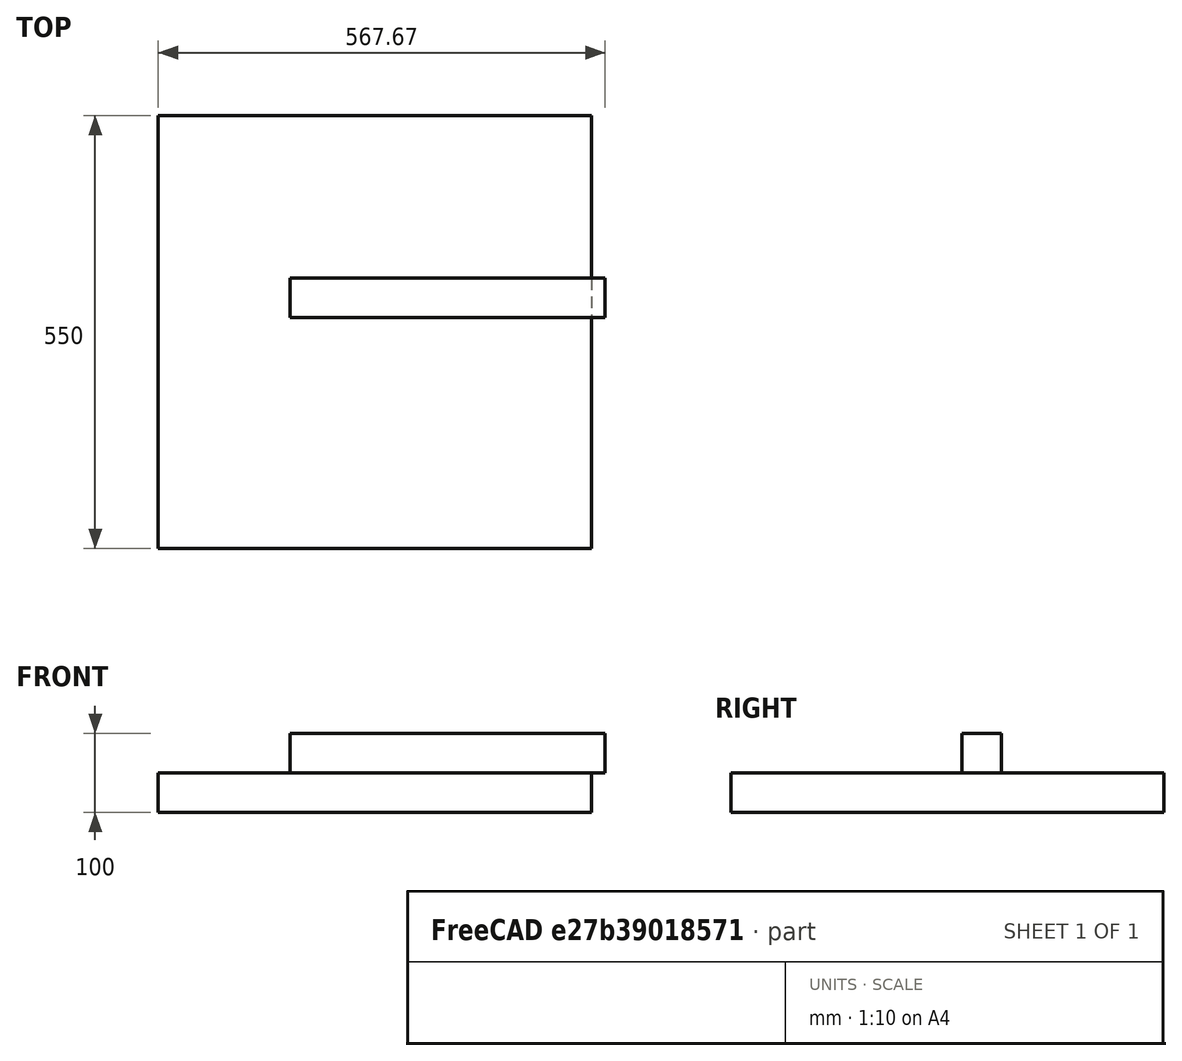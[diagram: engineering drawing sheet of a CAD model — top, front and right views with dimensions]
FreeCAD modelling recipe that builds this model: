
FCSTD DOCUMENT  (FreeCAD 1.0R38806 (Git))
Label: mesa_Ikea
License: All rights reserved
LicenseURL: https://en.wikipedia.org/wiki/All_rights_reserved
objects: App::Link×5, App::FeaturePython×5, Sketcher::SketchObject×2, PartDesign::Pad×2, PartDesign::Body×2, App::Part×2, App::DocumentObjectGroup×1, Assembly::JointGroup×1, Assembly::AssemblyObject×1
note: 12 computed .brp shape members not serialized (recipe doc carries the construction recipe); baked Part::Feature solids carry a one-line shape summary decoded from their .brp

FEATURE [Sketcher::SketchObject] Sketch
  ArcFitTolerance = 1e-06
  AttachmentSupport = -> [YZ_Plane]
  FullyConstrained = false
  MakeInternals = false
  MapMode = 5
  Placement = pos=(0,0,0) rot=(0.57735,0.57735,0.57735;2.0944rad)
  sketch-geometry (4):
    g0: LineSegment StartX=-305.851 StartY=309.369 StartZ=0 EndX=-305.851 EndY=-240.631 EndZ=0
    g1: LineSegment StartX=-305.851 StartY=-240.631 StartZ=0 EndX=244.149 EndY=-240.631 EndZ=0
    g2: LineSegment StartX=244.149 StartY=-240.631 StartZ=0 EndX=244.149 EndY=309.369 EndZ=0
    g3: LineSegment StartX=244.149 StartY=309.369 StartZ=0 EndX=-305.851 EndY=309.369 EndZ=0
  constraints (10):
    c: Coincident(g0,g1)
    c: Coincident(g1,g2)
    c: Coincident(g2,g3)
    c: Coincident(g3,g0)
    c: Vertical(g0)
    c: Vertical(g2)
    c: Horizontal(g1)
    c: Horizontal(g3)
    c: DistanceY(g2,g2) = 550
    c: DistanceX(g1,g1) = 550
FEATURE [PartDesign::Pad] Pad
  Direction = (1,0,0)
  Length = 50
  Length2 = 10
  Placement = pos=(0,0,0) rot=(1,1,1;2.0944rad)
  Profile = -> Sketch
  ReferenceAxis = -> Sketch [N_Axis]
  Refine = true
  Suppressed = false
  Type = 0
FEATURE [PartDesign::Body] Body  label="Boceto tablero"
  AllowCompound = false
  Group = -> [Sketch,Pad]
  Origin = -> Origin001
  Placement = pos=(0,0,0) rot=(0,1,0;1.5708rad)
  Tip = -> Pad
FEATURE [App::Part] Part  label="Tablero"
  Group = -> [Body]
  Origin = -> Origin
FEATURE [Sketcher::SketchObject] Sketch003
  ArcFitTolerance = 1e-06
  AttachmentSupport = -> [XY_Plane003]
  FullyConstrained = false
  MakeInternals = false
  MapMode = 5
  sketch-geometry (4):
    g0: LineSegment StartX=-72.9598 StartY=37.5082 StartZ=0 EndX=-72.9598 EndY=-12.4918 EndZ=0
    g1: LineSegment StartX=-72.9598 StartY=-12.4918 StartZ=0 EndX=327.04 EndY=-12.4918 EndZ=0
    g2: LineSegment StartX=327.04 StartY=-12.4918 StartZ=0 EndX=327.04 EndY=37.5082 EndZ=0
    g3: LineSegment StartX=327.04 StartY=37.5082 StartZ=0 EndX=-72.9598 EndY=37.5082 EndZ=0
  constraints (10):
    c: Coincident(g0,g1)
    c: Coincident(g1,g2)
    c: Coincident(g2,g3)
    c: Coincident(g3,g0)
    c: Vertical(g0)
    c: Vertical(g2)
    c: Horizontal(g1)
    c: Horizontal(g3)
    c: Distance(g0,g2) = 400
    c: Distance(g1,g3) = 50
FEATURE [PartDesign::Pad] Pad002
  Direction = (0,0,1)
  Length = 50
  Length2 = 10
  Profile = -> Sketch003
  ReferenceAxis = -> Sketch003 [N_Axis]
  Refine = true
  Suppressed = false
  Type = 0
FEATURE [PartDesign::Body] Body001  label="Body"
  AllowCompound = false
  Group = -> [Sketch003,Pad002]
  Origin = -> Origin003
  Tip = -> Pad002
FEATURE [App::Part] Part001  label="pata"
  Group = -> [Body001]
  Origin = -> Origin002
FEATURE [App::DocumentObjectGroup] Group  label="Modelado 3Dç"
  Group = -> [Part,Part001]
FEATURE [App::Link] Tablero  label="Tablero001"
  LinkedObject = -> Part
FEATURE [App::Link] pata  label="pata001"
  LinkPlacement = pos=(-240.631,-293.359,-97.9598) rot=(0,1,0;1.5708rad)
  LinkedObject = -> Part001
  Placement = pos=(-240.631,-293.359,-97.9598) rot=(0,1,0;1.5708rad)
FEATURE [App::Link] pata001  label="pata002"
  LinkPlacement = pos=(259.369,-293.359,-97.9598) rot=(0,1,0;1.5708rad)
  LinkedObject = -> Part001
  Placement = pos=(259.369,-293.359,-97.9598) rot=(0,1,0;1.5708rad)
FEATURE [App::Link] pata002  label="pata003"
  LinkPlacement = pos=(309.369,231.657,-122.96) rot=(0.707107,0,-0.707107;3.14159rad)
  LinkedObject = -> Part001
  Placement = pos=(309.369,231.657,-122.96) rot=(0.707107,0,-0.707107;3.14159rad)
FEATURE [App::Link] pata003  label="pata004"
  LinkPlacement = pos=(-190.631,206.641,-377.04) rot=(0,1,0;4.71239rad)
  LinkedObject = -> Part001
  Placement = pos=(-190.631,206.641,-377.04) rot=(0,1,0;4.71239rad)
FEATURE [App::FeaturePython] GroundedJoint  # Assembly grounded joint (typed FeaturePython)
  ObjectToGround = -> Tablero
FEATURE [App::FeaturePython] Fixed  # Assembly joint (typed FeaturePython)
  Activated = true
  AngleMax = 0
  AngleMin = 0
  Detach1 = false
  Detach2 = false
  Distance = 0
  Distance2 = 0
  EnableAngleMax = false
  EnableAngleMin = false
  EnableLengthMax = false
  EnableLengthMin = false
  JointType = 0 (Fixed)
  LengthMax = 0
  LengthMin = 0
  Placement1 = pos=(-72.9598,-12.4918,50) rot=(0.707107,0,0.707107;3.14159rad)
  Placement2 = pos=(25,-305.851,309.369) rot=(0.707107,0,0.707107;3.14159rad)
  Reference1 = -> Assembly [pata001.Body001.Pad002.Edge7,pata001.Body001.Pad002.Vertex4]
  Reference2 = -> Assembly [Tablero.Body.Pad.Edge1,Tablero.Body.Pad.Edge1]
FEATURE [App::FeaturePython] Fixed001  # Assembly joint (typed FeaturePython)
  Activated = true
  AngleMax = 0
  AngleMin = 0
  Detach1 = false
  Detach2 = false
  Distance = 0
  Distance2 = 0
  EnableAngleMax = false
  EnableAngleMin = false
  EnableLengthMax = false
  EnableLengthMin = false
  JointType = 0 (Fixed)
  LengthMax = 0
  LengthMin = 0
  Placement1 = pos=(-72.9598,-12.4918,0) rot=(0.707107,0,0.707107;3.14159rad)
  Placement2 = pos=(25,-305.851,-240.631) rot=(0.707107,0,0.707107;3.14159rad)
  Reference1 = -> Assembly [pata.Body001.Pad002.Edge6,pata.Body001.Pad002.Vertex3]
  Reference2 = -> Assembly [Tablero.Body.Pad.Edge2,Tablero.Body.Pad.Edge2]
FEATURE [App::FeaturePython] Fixed002  # Assembly joint (typed FeaturePython)
  Activated = true
  AngleMax = 0
  AngleMin = 0
  Detach1 = false
  Detach2 = false
  Distance = 0
  Distance2 = 0
  EnableAngleMax = false
  EnableAngleMin = false
  EnableLengthMax = false
  EnableLengthMin = false
  JointType = 0 (Fixed)
  LengthMax = 0
  LengthMin = 0
  Placement1 = pos=(327.04,37.5082,50) rot=(-0.707107,0,0.707107;3.14159rad)
  Placement2 = pos=(50,244.149,-240.631) rot=(0.707107,0,0.707107;3.14159rad)
  Reference1 = -> Assembly [pata003.Body001.Pad002.Edge12,pata003.Body001.Pad002.Vertex8]
  Reference2 = -> Assembly [Tablero.Body.Pad.Edge5,Tablero.Body.Pad.Vertex6]
FEATURE [App::FeaturePython] Fixed003  # Assembly joint (typed FeaturePython)
  Activated = true
  AngleMax = 0
  AngleMin = 0
  Detach1 = false
  Detach2 = false
  Distance = 0
  Distance2 = 0
  EnableAngleMax = false
  EnableAngleMin = false
  EnableLengthMax = false
  EnableLengthMin = false
  JointType = 0 (Fixed)
  LengthMax = 0
  LengthMin = 0
  Offset2 = pos=(0,0,0) rot=(0,0,1;3.14159rad)
  Placement1 = pos=(-72.9598,-12.4918,0) rot=(0.707107,0,0.707107;3.14159rad)
  Placement2 = pos=(50,244.149,309.369) rot=(0,-1,0;4.71239rad)
  Reference1 = -> Assembly [pata002.Body001.Pad002.Edge6,pata002.Body001.Pad002.Vertex3]
  Reference2 = -> Assembly [Tablero.Body.Pad.Edge8,Tablero.Body.Pad.Vertex8]
FEATURE [Assembly::JointGroup] Joints
  Group = -> [GroundedJoint,Fixed,Fixed001,Fixed002,Fixed003]
FEATURE [Assembly::AssemblyObject] Assembly
  Group = -> [Joints,Tablero,pata,pata001,pata002,pata003,GroundedJoint,Fixed,Fixed001,Fixed002,Fixed003]
  Origin = -> Origin004
  Type = Assembly
